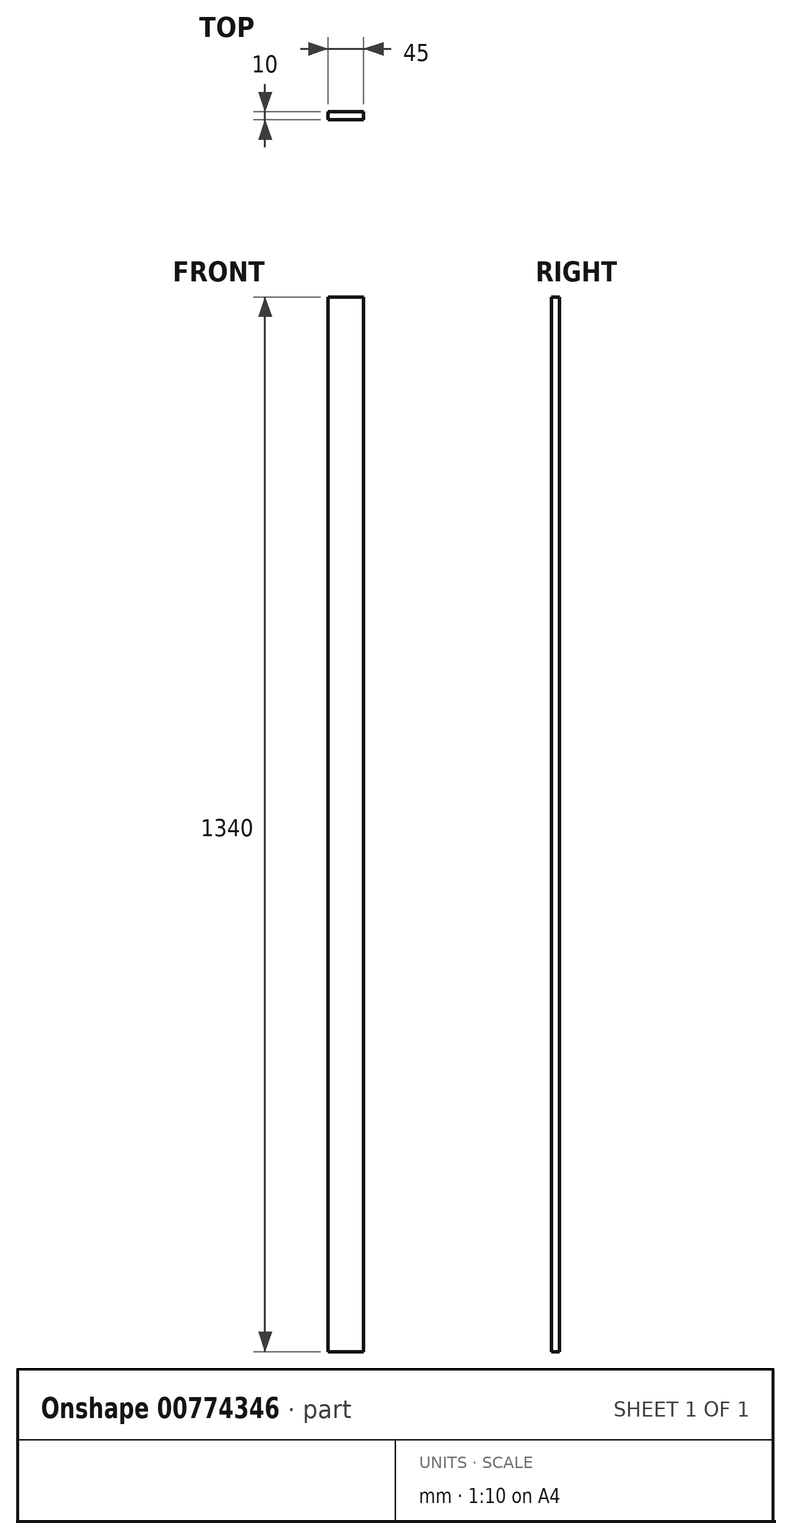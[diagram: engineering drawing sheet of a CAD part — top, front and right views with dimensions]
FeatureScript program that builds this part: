
annotation { "Feature Type Name" : "Feature", "Feature Type Description" : "" }
export const myFeature = defineFeature(function(context is Context, id is Id, definition is map)
    precondition{}
    {
        {
            var Q0;
            Q0=qCreatedBy(makeId("Top.planeOp"),FACE);
            var sketch = newSketch(context, id + "F0", { "sketchPlane" : qUnion([Q0])});
            skLineSegment(sketch, "E0.bottom", {"start": v(0, 0) * mm, "end": v(45, 0) * mm});
            skLineSegment(sketch, "E0.top", {"start": v(0, 10) * mm, "end": v(45, 10) * mm});
            skLineSegment(sketch, "E0.left", {"start": v(0, 0) * mm, "end": v(0, 10) * mm});
            skLineSegment(sketch, "E0.right", {"start": v(45, 0) * mm, "end": v(45, 10) * mm});
            skSolve(sketch);
        }
        {
            var Q0;
            Q0=makeQuery(id+"F0.imprint","IMPRINT",FACE,{"disambiguationData":[TD([[makeQuery(id+"F0.imprint","IMPRINT",EDGE,{"derivedFrom":sQuery(id+"F0.wireOp",EDGE,"E0.bottom")}),1.0]])]});
            extrude(context, id + "F1", {"entities" : qUnion([Q0]), "depth" : 1340 * mm, "offsetDistance" : 25 * mm});
        }
    });
